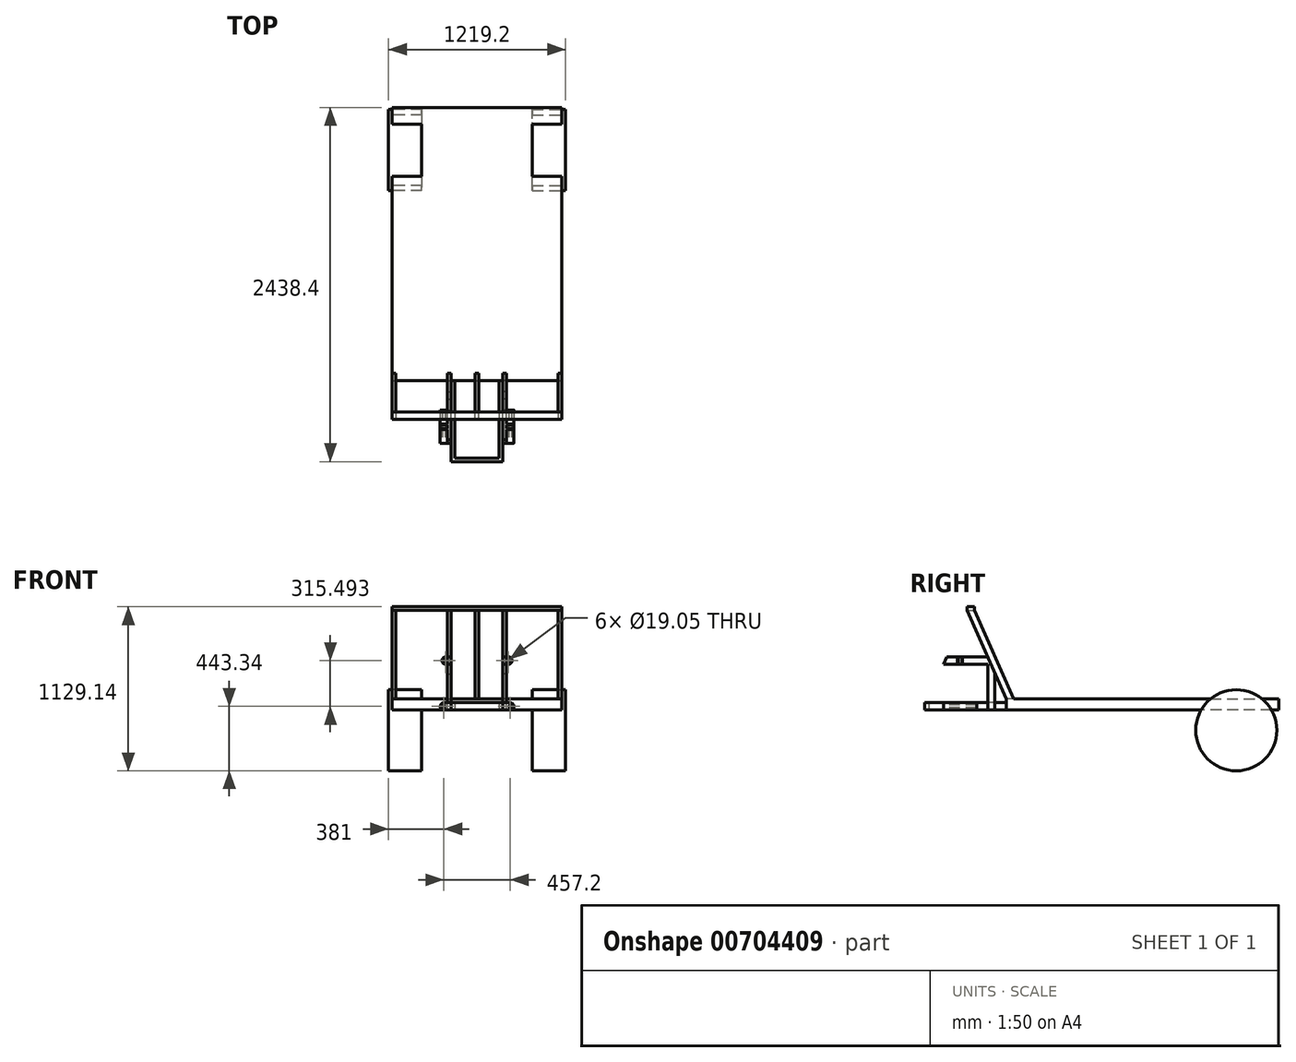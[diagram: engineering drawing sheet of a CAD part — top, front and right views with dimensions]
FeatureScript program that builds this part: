
annotation { "Feature Type Name" : "Feature", "Feature Type Description" : "" }
export const myFeature = defineFeature(function(context is Context, id is Id, definition is map)
    precondition{}
    {
        {
            var Q0;
            Q0=qCreatedBy(makeId("Top.planeOp"),FACE);
            var sketch = newSketch(context, id + "F0", { "sketchPlane" : qUnion([Q0])});
            skLineSegment(sketch, "E0.bottom", {"start": v(0, 0) * mm, "end": v(1168.4, 0) * mm});
            skLineSegment(sketch, "E0.top", {"start": v(0, 1879.6) * mm, "end": v(1168.4, 1879.6) * mm});
            skLineSegment(sketch, "E0.left", {"start": v(0, 0) * mm, "end": v(0, 1879.6) * mm});
            skLineSegment(sketch, "E0.right", {"start": v(1168.4, 0) * mm, "end": v(1168.4, 1879.6) * mm});
            skSolve(sketch);
        }
        {
            var Q0;
            Q0 = qSketchRegion(id + "F0", true);
            extrude(context, id + "F1", {"entities" : qUnion([Q0]), "depth" : 76.2 * mm, "offsetDistance" : 25.4 * mm});
        }
        {
            var Q0;
            Q0=makeQuery(id+"F1.opExtrude","SWEPT_FACE",FACE,{"disambiguationData":[OSD([sQuery(id+"F0.wireOp",EDGE,"E0.left")])]});
            var sketch = newSketch(context, id + "F2", { "sketchPlane" : qUnion([Q0])});
            skCircle(sketch, "E1", {"center": v(-1585.07, -138.54) * mm, "radius": 279.4 * mm});
            skSolve(sketch);
        }
        {
            var Q0;
            Q0 = qSketchRegion(id + "F2", true);
            extrude(context, id + "F3", {"entities" : qUnion([Q0]), "operationType" : NewBodyOperationType.ADD, "oppositeDirection" : true, "depth" : 203.2 * mm, "offsetDistance" : 25.4 * mm, "hasSecondDirection" : true, "secondDirectionOppositeDirection" : false, "secondDirectionDepth" : 25.4 * mm});
        }
        {
            var Q0;
            Q0=makeQuery(id+"F1.opExtrude","SWEPT_FACE",FACE,{"disambiguationData":[OSD([sQuery(id+"F0.wireOp",EDGE,"E0.right")])]});
            var sketch = newSketch(context, id + "F4", { "sketchPlane" : qUnion([Q0])});
            skLineSegment(sketch, "E2.0.0", {"start": v(1827.7, 0) * mm, "end": v(1342.43, 0) * mm});
            skArc(sketch, "E2.0.1", {"start": v(1342.43, 0) * mm, "mid": v(1585.07, -417.94) * mm, "end": v(1827.7, 0) * mm});
            skCircle(sketch, "E3.0.0", {"center": v(1585.07, -138.54) * mm, "radius": 279.4 * mm});
            skSolve(sketch);
        }
        {
            var Q0;
            Q0 = qSketchRegion(id + "F4", true);
            extrude(context, id + "F5", {"entities" : qUnion([Q0]), "operationType" : NewBodyOperationType.ADD, "oppositeDirection" : true, "depth" : 203.2 * mm, "offsetDistance" : 25.4 * mm, "hasSecondDirection" : true, "secondDirectionOppositeDirection" : false, "secondDirectionDepth" : 25.4 * mm});
        }
        {
            var Q0;
            Q0=makeQuery(id+"F1.opExtrude","CAP_FACE",FACE,{"disambiguationData":[OSD([sQuery(id+"F0.wireOp",EDGE,"E0.bottom"),sQuery(id+"F0.wireOp",EDGE,"E0.top"),sQuery(id+"F0.wireOp",EDGE,"E0.left"),sQuery(id+"F0.wireOp",EDGE,"E0.right")])],"isStart":true});
            var sketch = newSketch(context, id + "F6", { "sketchPlane" : qUnion([Q0])});
            skLineSegment(sketch, "E4", {"start": v(584.2, 0) * mm, "end": v(584.2, 847) * mm, "construction": true});
            skLineSegment(sketch, "E5.bottom", {"start": v(431.8, 0) * mm, "end": v(406.4, 0) * mm});
            skLineSegment(sketch, "E5.top", {"start": v(431.8, 558.8) * mm, "end": v(406.4, 558.8) * mm});
            skLineSegment(sketch, "E5.left", {"start": v(431.8, 0) * mm, "end": v(431.8, 558.8) * mm});
            skLineSegment(sketch, "E5.right", {"start": v(406.4, 0) * mm, "end": v(406.4, 558.8) * mm});
            skLineSegment(sketch, "E6.MirrorCS", {"start": v(762, 0) * mm, "end": v(762, 558.8) * mm});
            skLineSegment(sketch, "E7.MirrorCS", {"start": v(736.6, 558.8) * mm, "end": v(762, 558.8) * mm});
            skLineSegment(sketch, "E8.MirrorCS", {"start": v(736.6, 0) * mm, "end": v(762, 0) * mm});
            skLineSegment(sketch, "E9.MirrorCS", {"start": v(736.6, 0) * mm, "end": v(736.6, 558.8) * mm});
            skSolve(sketch);
        }
        {
            var Q0;
            Q0 = qSketchRegion(id + "F6", true);
            extrude(context, id + "F7", {"entities" : qUnion([Q0]), "operationType" : NewBodyOperationType.ADD, "oppositeDirection" : true, "depth" : 50.8 * mm, "offsetDistance" : 25.4 * mm});
        }
        {
            var Q0;
            {var subQ0=sQuery(id+"F0.wireOp",EDGE,"E0.bottom");var subQ2=sQuery(id+"F0.wireOp",EDGE,"E0.left");Q0=makeQuery(id+"F3.boolean.opBoolean","SPLIT",FACE,{"disambiguationData":[TD([makeQuery(id+"F1.opExtrude","SWEPT_FACE",FACE,{"disambiguationData":[OSD([subQ0])]})])],"derivedFrom":makeQuery(id+"F1.opExtrude","SWEPT_FACE",FACE,{"disambiguationData":[OSD([subQ2])]})});}
            var sketch = newSketch(context, id + "F8", { "sketchPlane" : qUnion([Q0])});
            skLineSegment(sketch, "E10", {"start": v(-50.8, 76.2) * mm, "end": v(216.08, 685.8) * mm});
            skLineSegment(sketch, "E11", {"start": v(216.08, 685.8) * mm, "end": v(266.88, 685.8) * mm});
            skLineSegment(sketch, "E12", {"start": v(266.88, 685.8) * mm, "end": v(0, 76.2) * mm});
            skLineSegment(sketch, "E13", {"start": v(0, 76.2) * mm, "end": v(-50.8, 76.2) * mm});
            skSolve(sketch);
        }
        {
            var Q0;
            Q0 = qSketchRegion(id + "F8", true);
            extrude(context, id + "F9", {"entities" : qUnion([Q0]), "operationType" : NewBodyOperationType.ADD, "oppositeDirection" : true, "depth" : 25.4 * mm, "offsetDistance" : 25.4 * mm});
        }
        {
            var Q0;
            {var subQ0=sQuery(id+"F0.wireOp",EDGE,"E0.bottom");var subQ1=sQuery(id+"F0.wireOp",EDGE,"E0.right");Q0=makeQuery(id+"F5.boolean.opBoolean","SPLIT",FACE,{"disambiguationData":[TD([makeQuery(id+"F1.opExtrude","SWEPT_FACE",FACE,{"disambiguationData":[OSD([subQ0])]})])],"derivedFrom":makeQuery(id+"F1.opExtrude","SWEPT_FACE",FACE,{"disambiguationData":[OSD([subQ1])]})});}
            var sketch = newSketch(context, id + "F10", { "sketchPlane" : qUnion([Q0])});
            skLineSegment(sketch, "E14.0.0", {"start": v(-266.88, 685.8) * mm, "end": v(0, 76.2) * mm});
            skLineSegment(sketch, "E14.0.1", {"start": v(0, 76.2) * mm, "end": v(50.8, 76.2) * mm});
            skLineSegment(sketch, "E14.0.2", {"start": v(50.8, 76.2) * mm, "end": v(-216.08, 685.8) * mm});
            skLineSegment(sketch, "E14.0.3", {"start": v(-216.08, 685.8) * mm, "end": v(-266.88, 685.8) * mm});
            skSolve(sketch);
        }
        {
            var Q0;
            Q0 = qSketchRegion(id + "F10", true);
            extrude(context, id + "F11", {"entities" : qUnion([Q0]), "operationType" : NewBodyOperationType.ADD, "oppositeDirection" : true, "depth" : 25.4 * mm, "offsetDistance" : 25.4 * mm});
        }
        {
            var Q0;
            {var subQ0=sQuery(id+"F0.wireOp",EDGE,"E0.bottom");var subQ1=sQuery(id+"F0.wireOp",EDGE,"E0.right");Q0=makeQuery(id+"F11.boolean.opBoolean","MERGE",FACE,{"derivedFrom":[makeQuery(id+"F5.boolean.opBoolean","SPLIT",FACE,{"disambiguationData":[TD([makeQuery(id+"F1.opExtrude","SWEPT_FACE",FACE,{"disambiguationData":[OSD([subQ0])]})])],"derivedFrom":makeQuery(id+"F1.opExtrude","SWEPT_FACE",FACE,{"disambiguationData":[OSD([subQ1])]})}),makeQuery(id+"F11.opExtrude","CAP_FACE",FACE,{"disambiguationData":[OSD([sQuery(id+"F10.wireOp",EDGE,"E14.0.0"),sQuery(id+"F10.wireOp",EDGE,"E14.0.1"),sQuery(id+"F10.wireOp",EDGE,"E14.0.2"),sQuery(id+"F10.wireOp",EDGE,"E14.0.3")])],"isStart":true})]});}
            var sketch = newSketch(context, id + "F12", { "sketchPlane" : qUnion([Q0])});
            skLineSegment(sketch, "E15.bottom", {"start": v(-216.08, 685.8) * mm, "end": v(-266.88, 685.8) * mm});
            skLineSegment(sketch, "E15.top", {"start": v(-216.08, 711.2) * mm, "end": v(-266.88, 711.2) * mm});
            skLineSegment(sketch, "E15.left", {"start": v(-216.08, 685.8) * mm, "end": v(-216.08, 711.2) * mm});
            skLineSegment(sketch, "E15.right", {"start": v(-266.88, 685.8) * mm, "end": v(-266.88, 711.2) * mm});
            skSolve(sketch);
        }
        {
            var Q0;
            Q0 = qSketchRegion(id + "F12", true);
            var Q1;
            {var subQ0=sQuery(id+"F0.wireOp",EDGE,"E0.bottom");var subQ2=sQuery(id+"F0.wireOp",EDGE,"E0.left");Q1=makeQuery(id+"F9.boolean.opBoolean","MERGE",FACE,{"derivedFrom":[makeQuery(id+"F3.boolean.opBoolean","SPLIT",FACE,{"disambiguationData":[TD([makeQuery(id+"F1.opExtrude","SWEPT_FACE",FACE,{"disambiguationData":[OSD([subQ0])]})])],"derivedFrom":makeQuery(id+"F1.opExtrude","SWEPT_FACE",FACE,{"disambiguationData":[OSD([subQ2])]})}),makeQuery(id+"F9.opExtrude","CAP_FACE",FACE,{"disambiguationData":[OSD([sQuery(id+"F8.wireOp",EDGE,"E10"),sQuery(id+"F8.wireOp",EDGE,"E11"),sQuery(id+"F8.wireOp",EDGE,"E12"),sQuery(id+"F8.wireOp",EDGE,"E13")])],"isStart":true})]});}
            extrude(context, id + "F13", {"entities" : qUnion([Q0]), "operationType" : NewBodyOperationType.ADD, "endBound" : BoundingType.UP_TO_SURFACE, "oppositeDirection" : true, "depth" : 25.4 * mm, "endBoundEntityFace" : qUnion([Q1]), "offsetDistance" : 25.4 * mm});
        }
        {
            var Q0;
            Q0=makeQuery(id+"F1.opExtrude","SWEPT_FACE",FACE,{"disambiguationData":[OSD([sQuery(id+"F0.wireOp",EDGE,"E0.bottom")])]});
            var sketch = newSketch(context, id + "F14", { "sketchPlane" : qUnion([Q0])});
            skLineSegment(sketch, "E16", {"start": v(584.2, 0) * mm, "end": v(584.2, 76.2) * mm, "construction": true});
            skSolve(sketch);
        }
        {
            var Q0;
            Q0=qCreatedBy(makeId("Right.planeOp"),FACE);
            var Q1;
            Q1=sQuery(id+"F14.wireOp",EDGE,"E16");
            cPlane(context, id + "F15", {"entities" : qUnion([Q0, Q1]), "cplaneType" : CPlaneType.LINE_ANGLE, "offset" : 25.4 * mm, "angle" : 0 * degree, "width" : 152.4 * mm, "height" : 152.4 * mm});
        }
        {
            var Q0;
            Q0=qCreatedBy(id+"F15.planeOp",FACE);
            var sketch = newSketch(context, id + "F16", { "sketchPlane" : qUnion([Q0])});
            skLineSegment(sketch, "E17.0.0", {"start": v(-50.8, 76.2) * mm, "end": v(0, 76.2) * mm});
            skLineSegment(sketch, "E17.0.1", {"start": v(0, 76.2) * mm, "end": v(266.88, 685.8) * mm});
            skLineSegment(sketch, "E17.0.2", {"start": v(266.88, 685.8) * mm, "end": v(216.08, 685.8) * mm});
            skLineSegment(sketch, "E17.0.3", {"start": v(216.08, 685.8) * mm, "end": v(-50.8, 76.2) * mm});
            skSolve(sketch);
        }
        {
            var Q0;
            Q0 = qSketchRegion(id + "F16", true);
            extrude(context, id + "F17", {"entities" : qUnion([Q0]), "operationType" : NewBodyOperationType.ADD, "depth" : 12.7 * mm, "offsetDistance" : 25.4 * mm, "hasSecondDirection" : true, "secondDirectionOppositeDirection" : true, "secondDirectionDepth" : 12.7 * mm});
        }
        {
            var Q0;
            Q0=makeQuery(id+"F7.opExtrude","SWEPT_FACE",FACE,{"disambiguationData":[OSD([sQuery(id+"F6.wireOp",EDGE,"E5.right")])]});
            var sketch = newSketch(context, id + "F18", { "sketchPlane" : qUnion([Q0])});
            skLineSegment(sketch, "E18.bottom", {"start": v(203.2, 0) * mm, "end": v(431.8, 0) * mm});
            skLineSegment(sketch, "E18.top", {"start": v(203.2, 50.8) * mm, "end": v(431.8, 50.8) * mm});
            skLineSegment(sketch, "E18.left", {"start": v(203.2, 0) * mm, "end": v(203.2, 50.8) * mm});
            skLineSegment(sketch, "E18.right", {"start": v(431.8, 0) * mm, "end": v(431.8, 50.8) * mm});
            skSolve(sketch);
        }
        {
            var Q0;
            Q0 = qSketchRegion(id + "F18", true);
            extrude(context, id + "F19", {"entities" : qUnion([Q0]), "operationType" : NewBodyOperationType.ADD, "depth" : 76.2 * mm, "offsetDistance" : 25.4 * mm});
        }
        {
            var Q0;
            Q0=makeQuery(id+"F19.opExtrude","SWEPT_FACE",FACE,{"disambiguationData":[OSD([sQuery(id+"F18.wireOp",EDGE,"E18.right")])]});
            var sketch = newSketch(context, id + "F20", { "sketchPlane" : qUnion([Q0])});
            skLineSegment(sketch, "E19.0.0", {"start": v(406.4, 0) * mm, "end": v(406.4, 50.8) * mm});
            skLineSegment(sketch, "E19.0.1", {"start": v(406.4, 50.8) * mm, "end": v(355.6, 50.8) * mm});
            skLineSegment(sketch, "E19.0.2", {"start": v(330.2, 25.4) * mm, "end": v(330.2, 25.4) * mm});
            skLineSegment(sketch, "E19.0.3", {"start": v(355.6, 0) * mm, "end": v(406.4, 0) * mm});
            skPoint(sketch, "E20.visualSharp", {"position": v(330.2, 50.8) * mm});
            skArc(sketch, "E20.filletArc", {"start": v(355.6, 50.8) * mm, "mid": v(337.64, 43.36) * mm, "end": v(330.2, 25.4) * mm});
            skPoint(sketch, "E21.visualSharp", {"position": v(330.2, 0) * mm});
            skArc(sketch, "E21.filletArc", {"start": v(330.2, 25.4) * mm, "mid": v(337.64, 7.44) * mm, "end": v(355.6, 0) * mm});
            skCircle(sketch, "E22", {"center": v(355.6, 25.4) * mm, "radius": 9.53 * mm});
            skSolve(sketch);
        }
        {
            var Q0;
            {var subQ0=sQuery(id+"F20.wireOp",EDGE,"E20.filletArc");Q0=makeQuery(id+"F20.imprint","IMPRINT",FACE,{"disambiguationData":[TD([[makeQuery(id+"F20.imprint","IMPRINT",EDGE,{"derivedFrom":subQ0}),-1.0]])]});}
            var Q1;
            Q1=makeQuery(id+"F20.imprint","IMPRINT",FACE,{"disambiguationData":[TD([[makeQuery(id+"F20.imprint","IMPRINT",EDGE,{"derivedFrom":sQuery(id+"F20.wireOp",EDGE,"E22")}),1.0]])]});
            var Q2;
            {var subQ0=sQuery(id+"F20.wireOp",EDGE,"E21.filletArc");Q2=makeQuery(id+"F20.imprint","IMPRINT",FACE,{"disambiguationData":[TD([[makeQuery(id+"F20.imprint","IMPRINT",EDGE,{"derivedFrom":subQ0}),-1.0]])]});}
            extrude(context, id + "F21", {"entities" : qUnion([Q0, Q1, Q2]), "operationType" : NewBodyOperationType.REMOVE, "endBound" : BoundingType.UP_TO_NEXT, "oppositeDirection" : true, "depth" : 25.4 * mm, "offsetDistance" : 25.4 * mm});
        }
        {
            var Q0;
            {var subQ0=sQuery(id+"F6.wireOp",EDGE,"E5.right");var subQ4=sQuery(id+"F0.wireOp",EDGE,"E0.bottom");Q0=makeQuery(id+"F19.boolean.opBoolean","SPLIT",FACE,{"disambiguationData":[TD([makeQuery(id+"F1.opExtrude","SWEPT_FACE",FACE,{"disambiguationData":[OSD([subQ4])]})])],"derivedFrom":makeQuery(id+"F7.opExtrude","SWEPT_FACE",FACE,{"disambiguationData":[OSD([subQ0])]})});}
            var sketch = newSketch(context, id + "F22", { "sketchPlane" : qUnion([Q0])});
            skLineSegment(sketch, "E23.0.0", {"start": v(216.08, 685.8) * mm, "end": v(-50.8, 76.2) * mm});
            skLineSegment(sketch, "E23.0.1", {"start": v(-50.8, 76.2) * mm, "end": v(0, 76.2) * mm});
            skLineSegment(sketch, "E23.0.2", {"start": v(0, 76.2) * mm, "end": v(266.88, 685.8) * mm});
            skLineSegment(sketch, "E23.0.3", {"start": v(266.88, 685.8) * mm, "end": v(216.08, 685.8) * mm});
            skLineSegment(sketch, "E24", {"start": v(76.2, 0) * mm, "end": v(76.2, 366.3) * mm});
            skLineSegment(sketch, "E25", {"start": v(76.2, 0) * mm, "end": v(127, 0) * mm});
            skLineSegment(sketch, "E26", {"start": v(127, 0) * mm, "end": v(127, 482.33) * mm});
            skLineSegment(sketch, "E27", {"start": v(127, 482.33) * mm, "end": v(76.2, 366.3) * mm});
            skLineSegment(sketch, "E28.0", {"start": v(431.8, 50.8) * mm, "end": v(558.8, 50.8) * mm, "construction": true});
            skLineSegment(sketch, "E29.0.0", {"start": v(203.2, 50.8) * mm, "end": v(203.2, 0) * mm, "construction": true});
            skLineSegment(sketch, "E29.0.1", {"start": v(203.2, 0) * mm, "end": v(431.8, 0) * mm, "construction": true});
            skLineSegment(sketch, "E29.0.2", {"start": v(431.8, 0) * mm, "end": v(431.8, 50.8) * mm, "construction": true});
            skLineSegment(sketch, "E29.0.3", {"start": v(431.8, 50.8) * mm, "end": v(203.2, 50.8) * mm, "construction": true});
            skLineSegment(sketch, "E30.0", {"start": v(0, 50.8) * mm, "end": v(203.2, 50.8) * mm, "construction": true});
            skLineSegment(sketch, "E31", {"start": v(76.2, 366.3) * mm, "end": v(408.11, 366.3) * mm});
            skLineSegment(sketch, "E32", {"start": v(408.11, 366.3) * mm, "end": v(431.8, 315.5) * mm});
            skLineSegment(sketch, "E33", {"start": v(431.8, 315.5) * mm, "end": v(53.96, 315.5) * mm});
            skSolve(sketch);
        }
        {
            var Q0;
            Q0 = qSketchRegion(id + "F22", true);
            extrude(context, id + "F23", {"entities" : qUnion([Q0]), "operationType" : NewBodyOperationType.ADD, "depth" : 25.4 * mm, "offsetDistance" : 25.4 * mm});
        }
        {
            var Q0;
            Q0=makeQuery(id+"F23.opExtrude","CAP_FACE",FACE,{"disambiguationData":[OSD([sQuery(id+"F22.wireOp",EDGE,"E24"),sQuery(id+"F22.wireOp",EDGE,"E25"),sQuery(id+"F22.wireOp",EDGE,"E26"),sQuery(id+"F22.wireOp",EDGE,"E27"),sQuery(id+"F22.wireOp",EDGE,"E31"),sQuery(id+"F22.wireOp",EDGE,"E32"),sQuery(id+"F22.wireOp",EDGE,"E33")])],"isStart":false});
            var sketch = newSketch(context, id + "F24", { "sketchPlane" : qUnion([Q0])});
            skLineSegment(sketch, "E34.0.0", {"start": v(203.2, 50.8) * mm, "end": v(203.2, 0) * mm});
            skLineSegment(sketch, "E34.0.1", {"start": v(203.2, 0) * mm, "end": v(431.8, 0) * mm});
            skLineSegment(sketch, "E34.0.2", {"start": v(431.8, 0) * mm, "end": v(431.8, 50.8) * mm});
            skLineSegment(sketch, "E34.0.3", {"start": v(431.8, 50.8) * mm, "end": v(203.2, 50.8) * mm});
            skLineSegment(sketch, "E35", {"start": v(317.5, 50.8) * mm, "end": v(317.5, 366.3) * mm, "construction": true});
            skLineSegment(sketch, "E36", {"start": v(317.5, 366.3) * mm, "end": v(298.45, 366.3) * mm});
            skLineSegment(sketch, "E37", {"start": v(298.45, 366.3) * mm, "end": v(298.45, 315.5) * mm});
            skLineSegment(sketch, "E38", {"start": v(298.45, 315.5) * mm, "end": v(317.5, 315.5) * mm});
            skLineSegment(sketch, "E39", {"start": v(304.8, 366.3) * mm, "end": v(304.8, 315.5) * mm});
            skLineSegment(sketch, "E40.MirrorCS", {"start": v(330.2, 366.3) * mm, "end": v(330.2, 315.5) * mm});
            skLineSegment(sketch, "E41.MirrorCS", {"start": v(336.55, 315.5) * mm, "end": v(317.5, 315.5) * mm});
            skLineSegment(sketch, "E42.MirrorCS", {"start": v(336.55, 366.3) * mm, "end": v(336.55, 315.5) * mm});
            skLineSegment(sketch, "E43.MirrorCS", {"start": v(317.5, 366.3) * mm, "end": v(336.55, 366.3) * mm});
            skSolve(sketch);
        }
        {
            var Q0;
            {var subQ0=sQuery(id+"F24.wireOp",EDGE,"E37");Q0=makeQuery(id+"F24.imprint","IMPRINT",FACE,{"disambiguationData":[TD([[makeQuery(id+"F24.imprint","IMPRINT",EDGE,{"derivedFrom":subQ0}),1.0]])]});}
            var Q1;
            {var subQ0=sQuery(id+"F24.wireOp",EDGE,"E40.MirrorCS");Q1=makeQuery(id+"F24.imprint","IMPRINT",FACE,{"disambiguationData":[TD([[makeQuery(id+"F24.imprint","IMPRINT",EDGE,{"derivedFrom":subQ0}),1.0]])]});}
            extrude(context, id + "F25", {"entities" : qUnion([Q0, Q1]), "operationType" : NewBodyOperationType.ADD, "depth" : 38.1 * mm, "offsetDistance" : 25.4 * mm});
        }
        {
            var Q0;
            Q0=makeQuery(id+"F25.opExtrude","SWEPT_FACE",FACE,{"disambiguationData":[OSD([sQuery(id+"F24.wireOp",EDGE,"E42.MirrorCS")])]});
            var sketch = newSketch(context, id + "F26", { "sketchPlane" : qUnion([Q0])});
            skLineSegment(sketch, "E44.0.0", {"start": v(381, 315.5) * mm, "end": v(381, 366.3) * mm});
            skLineSegment(sketch, "E44.0.1", {"start": v(381, 366.3) * mm, "end": v(368.3, 366.3) * mm});
            skLineSegment(sketch, "E44.0.2", {"start": v(342.9, 340.9) * mm, "end": v(342.9, 340.9) * mm});
            skLineSegment(sketch, "E44.0.3", {"start": v(368.3, 315.5) * mm, "end": v(381, 315.5) * mm});
            skPoint(sketch, "E45.visualSharp", {"position": v(342.9, 366.3) * mm});
            skArc(sketch, "E45.filletArc", {"start": v(368.3, 366.3) * mm, "mid": v(350.34, 358.85) * mm, "end": v(342.9, 340.9) * mm});
            skPoint(sketch, "E46.visualSharp", {"position": v(342.9, 315.5) * mm});
            skArc(sketch, "E46.filletArc", {"start": v(342.9, 340.9) * mm, "mid": v(350.34, 322.93) * mm, "end": v(368.3, 315.5) * mm});
            skCircle(sketch, "E47", {"center": v(368.3, 340.9) * mm, "radius": 9.53 * mm});
            skSolve(sketch);
        }
        {
            var Q0;
            {var subQ0=sQuery(id+"F26.wireOp",EDGE,"E45.filletArc");Q0=makeQuery(id+"F26.imprint","IMPRINT",FACE,{"disambiguationData":[TD([[makeQuery(id+"F26.imprint","IMPRINT",EDGE,{"derivedFrom":subQ0}),-1.0]])]});}
            var Q1;
            Q1=makeQuery(id+"F26.imprint","IMPRINT",FACE,{"disambiguationData":[TD([[makeQuery(id+"F26.imprint","IMPRINT",EDGE,{"derivedFrom":sQuery(id+"F26.wireOp",EDGE,"E47")}),1.0]])]});
            var Q2;
            {var subQ0=sQuery(id+"F26.wireOp",EDGE,"E46.filletArc");Q2=makeQuery(id+"F26.imprint","IMPRINT",FACE,{"disambiguationData":[TD([[makeQuery(id+"F26.imprint","IMPRINT",EDGE,{"derivedFrom":subQ0}),-1.0]])]});}
            extrude(context, id + "F27", {"entities" : qUnion([Q0, Q1, Q2]), "operationType" : NewBodyOperationType.REMOVE, "oppositeDirection" : true, "depth" : 50.8 * mm, "offsetDistance" : 25.4 * mm});
        }
        {
            var Q0;
            Q0=makeQuery(id+"F1.opExtrude","SWEPT_BODY",BODY,{"disambiguationData":[OSD([sQuery(id+"F0.wireOp",EDGE,"E0.bottom"),sQuery(id+"F0.wireOp",EDGE,"E0.top"),sQuery(id+"F0.wireOp",EDGE,"E0.left"),sQuery(id+"F0.wireOp",EDGE,"E0.right")])]});
            var Q1;
            Q1=qCreatedBy(id+"F15.planeOp",FACE);
            mirror(context, id + "F28", {"operationType" : NewBodyOperationType.ADD, "entities" : qUnion([Q0]), "mirrorPlane" : qUnion([Q1])});
        }
        {
            var Q0;
            Q0=makeQuery(id+"F7.opExtrude","SWEPT_FACE",FACE,{"disambiguationData":[OSD([sQuery(id+"F6.wireOp",EDGE,"E9.MirrorCS")])]});
            var sketch = newSketch(context, id + "F29", { "sketchPlane" : qUnion([Q0])});
            skLineSegment(sketch, "E48.bottom", {"start": v(558.8, 50.8) * mm, "end": v(533.4, 50.8) * mm});
            skLineSegment(sketch, "E48.top", {"start": v(558.8, 0) * mm, "end": v(533.4, 0) * mm});
            skLineSegment(sketch, "E48.left", {"start": v(558.8, 50.8) * mm, "end": v(558.8, 0) * mm});
            skLineSegment(sketch, "E48.right", {"start": v(533.4, 50.8) * mm, "end": v(533.4, 0) * mm});
            skSolve(sketch);
        }
        {
            var Q0;
            Q0 = qSketchRegion(id + "F29", true);
            extrude(context, id + "F30", {"entities" : qUnion([Q0]), "operationType" : NewBodyOperationType.ADD, "endBound" : BoundingType.UP_TO_NEXT, "depth" : 25.4 * mm, "offsetDistance" : 25.4 * mm});
        }
    });
